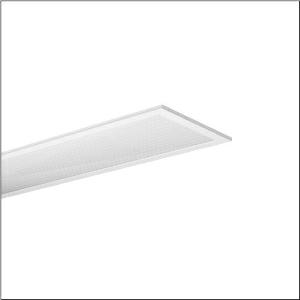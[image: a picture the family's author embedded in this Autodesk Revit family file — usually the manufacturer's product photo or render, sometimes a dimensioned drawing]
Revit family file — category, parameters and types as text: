
# Revit family: apollon_r__21_linear_51mq17wd2412_9bf3
name_source: partatom
category: Lighting Fixtures
units: mm (PartAtom-declared; Revit-internal decimal feet)

## family parameters
Cut with Voids When Loaded = No
Host = Face
Light Source = No
Part Type = Normal
Room Calculation Point = No
Round Connector Dimension = Use Diameter
Shared = No

## types (1)
- Apollon® 21 linear (1 x LED, 7200 lm, 60 W, 4000K)
    Apparent Load = 60 VA
    CIE Flux Codes = 61 87 97 100 100
    Color Rendering = 80
    Color Temperature = 4000K
    Default Elevation = 1800 mm
    Description = Apollon® 21 linear, office luminaire, primary optical cover: micro prismatic cover, CAT 2 (L<= 3000cd/m²), light emission: direct distribution, primary light characteristic: symmetric, installation type: lay-in mounting, LED, rated luminous flux: 7.200lm, luminous efficacy: 120lm/W, light colour: 840, colour temperature: 4000K, control gear: ECG DALI, with terminal, 5-pole, mains connection: 220..240V, AC, 50/60Hz, rated input power: 60W, housing, of aluminium, coated, pure white, length: 1.545mm, width: 307mm, height: 48mm, housing upper side, of sheet steel, galvanised, protection rating (complete): IP20, protection rating (lamp compartment, on room side): IP50, insulation class (complete): insulation class I (protective earthing), certification: CE, ENEC, packaging unit: 1 piece
    Height = 0 mm  [stored 0 ft]
    Lamp = 1 x LED
    Lamp Light Flux = 7200 lm
    Lamp Power = 60 W
    Lamp count = 1
    Length = 1545 mm
    Luminous efficacy = 120 lm/W
    Manufacturer = Siteco
    ModVariant = No
    Model = 51MQ17WD2412
    Mounting Place = Ceiling
    Mounting Type = Recessed
    Number of Poles = 1
    OnlyDefault = Yes
    Power Factor = 1
    Product Name = Apollon® 21 linear
    Product group = office luminaire | ceiling recessed
    ProductGroupID = 401
    Protection Class = Protection class I
    Protection Degree = IP 20
    RLX_Detail_Level = 1
    RLX_Emergency_Light_Flux = 0 lm
    RLX_Emergency_Type = 0
    RLX_Emergency_Type_DB = No
    RlxData = <blob elided: 17269 chars, md5=9eb82b1f>
    Socket = socket
    Standby Power = 0 W
    System Light Flux = 7200 lm
    System Power = 60 W
    Type Comments = Product without accessories
    Type Image = l_1291045.jpg
    URL = http://relux.com
    VarID = ---
    Voltage = 0 V
    Weight = 0.00 kg
    Width = 307 mm

note: [stored X ft] marks values corroborated as IEEE doubles in the binary element streams (Revit-internal decimal feet)

## geometry (parser evidence)
native form markers: Blend x4, Sweep x10
no freeform markers — native parametric forms only
